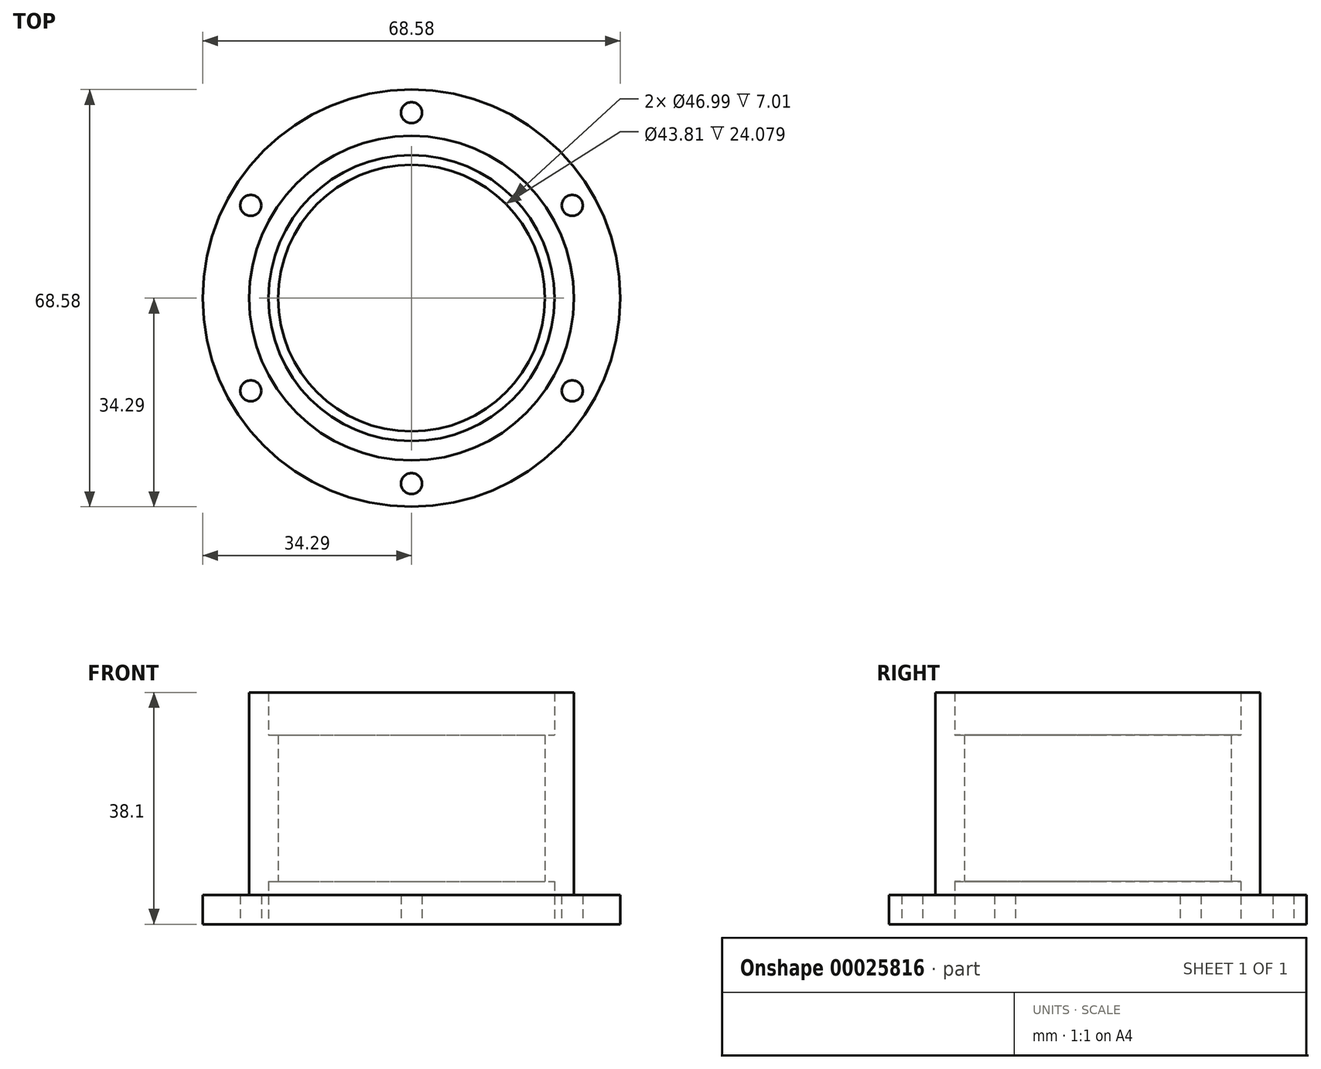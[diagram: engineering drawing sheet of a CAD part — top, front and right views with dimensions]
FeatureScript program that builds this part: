
annotation { "Feature Type Name" : "Feature", "Feature Type Description" : "" }
export const myFeature = defineFeature(function(context is Context, id is Id, definition is map)
    precondition{}
    {
        {
            var Q0;
            Q0=qCreatedBy(makeId("Front.planeOp"),FACE);
            var sketch = newSketch(context, id + "F0", { "sketchPlane" : qUnion([Q0])});
            skLineSegment(sketch, "E0", {"start": v(0, 0) * mm, "end": v(0, 39.33) * mm, "construction": true});
            skLineSegment(sketch, "E1", {"start": v(0, 0) * mm, "end": v(-23.5, 0) * mm, "construction": true});
            skLineSegment(sketch, "E2", {"start": v(-23.5, 0) * mm, "end": v(-34.3, 0) * mm});
            skLineSegment(sketch, "E3", {"start": v(-34.3, 0) * mm, "end": v(-34.3, 4.78) * mm});
            skLineSegment(sketch, "E4", {"start": v(-34.29, 4.78) * mm, "end": v(-26.67, 4.78) * mm});
            skLineSegment(sketch, "E5", {"start": v(-26.67, 4.78) * mm, "end": v(-26.67, 38.1) * mm});
            skLineSegment(sketch, "E6", {"start": v(-26.67, 38.1) * mm, "end": v(-23.5, 38.1) * mm});
            skLineSegment(sketch, "E7", {"start": v(-23.5, 38.1) * mm, "end": v(-23.5, 31.09) * mm});
            skLineSegment(sketch, "E8", {"start": v(-23.5, 31.09) * mm, "end": v(-21.9, 31.09) * mm});
            skLineSegment(sketch, "E9", {"start": v(-21.9, 31.09) * mm, "end": v(-21.9, 7.01) * mm});
            skLineSegment(sketch, "E10", {"start": v(-21.9, 7.01) * mm, "end": v(-23.5, 7.01) * mm});
            skLineSegment(sketch, "E11", {"start": v(-23.5, 7.01) * mm, "end": v(-23.5, 0) * mm});
            skSolve(sketch);
        }
        {
            var Q0;
            Q0=makeQuery(id+"F0.imprint","IMPRINT",FACE,{"disambiguationData":[TD([[makeQuery(id+"F0.imprint","IMPRINT",EDGE,{"derivedFrom":sQuery(id+"F0.wireOp",EDGE,"E2")}),-1.0]])]});
            var Q1;
            Q1=sQuery(id+"F0.wireOp",EDGE,"E0");
            revolve(context, id + "F1", {"entities" : qUnion([Q0]), "axis" : qUnion([Q1]), "revolveType" : RevolveType.FULL});
        }
        {
            var Q0;
            Q0=makeQuery(id+"F1.opRevolve","SWEPT_FACE",FACE,{"disambiguationData":[OSD([sQuery(id+"F0.wireOp",EDGE,"E2")])]});
            var sketch = newSketch(context, id + "F2", { "sketchPlane" : qUnion([Q0])});
            skLineSegment(sketch, "E12", {"start": v(0, 0) * mm, "end": v(0, 30.48) * mm});
            skLineSegment(sketch, "E13.1.0", {"start": v(0, 0) * mm, "end": v(-26.4, 15.24) * mm});
            skLineSegment(sketch, "E13.2.0", {"start": v(0, 0) * mm, "end": v(-26.4, -15.24) * mm});
            skPoint(sketch, "E13.center", {"position": v(0, 0) * mm});
            skLineSegment(sketch, "E14.1.3.0", {"start": v(0, 0) * mm, "end": v(0, -30.48) * mm});
            skLineSegment(sketch, "E14.1.4.0", {"start": v(0, 0) * mm, "end": v(26.4, -15.24) * mm});
            skLineSegment(sketch, "E14.1.5.0", {"start": v(0, 0) * mm, "end": v(26.4, 15.24) * mm});
            skSolve(sketch);
        }
        {
            var Q0;
            Q0=sQuery(id+"F2.wireOp",VERTEX,"E13.1.0.end");
            var Q1;
            Q1=sQuery(id+"F2.wireOp",VERTEX,"E12.end");
            var Q2;
            Q2=sQuery(id+"F2.wireOp",VERTEX,"E14.1.5.0.end");
            var Q3;
            Q3=sQuery(id+"F2.wireOp",VERTEX,"E14.1.4.0.end");
            var Q4;
            Q4=sQuery(id+"F2.wireOp",VERTEX,"E14.1.3.0.end");
            var Q5;
            Q5=sQuery(id+"F2.wireOp",VERTEX,"E13.2.0.end");
            var Q6;
            Q6=makeQuery(id+"F1.opRevolve","SWEPT_BODY",BODY,{"disambiguationData":[OSD([sQuery(id+"F0.wireOp",EDGE,"E2"),sQuery(id+"F0.wireOp",EDGE,"E3"),sQuery(id+"F0.wireOp",EDGE,"E4"),sQuery(id+"F0.wireOp",EDGE,"E5"),sQuery(id+"F0.wireOp",EDGE,"E6"),sQuery(id+"F0.wireOp",EDGE,"E7"),sQuery(id+"F0.wireOp",EDGE,"E8"),sQuery(id+"F0.wireOp",EDGE,"E9"),sQuery(id+"F0.wireOp",EDGE,"E10"),sQuery(id+"F0.wireOp",EDGE,"E11")])]});
            hole(context, id + "F3", {"style" : HoleStyle.SIMPLE, "holeDiameter" : 3.45 * mm, "endStyle" : HoleEndStyle.THROUGH, "locations" : qUnion([Q0, Q1, Q2, Q3, Q4, Q5]), "scope" : qUnion([Q6])});
        }
    });
